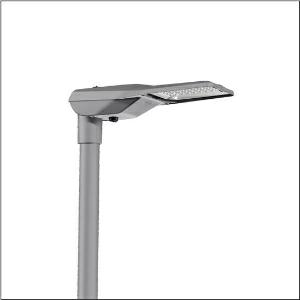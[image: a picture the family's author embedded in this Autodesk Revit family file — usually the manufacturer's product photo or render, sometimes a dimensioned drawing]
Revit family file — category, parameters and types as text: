
# Revit family: streetlight_sl_21_iq_mini___st0_8a_5xe2c31y08hb_5d56
name_source: partatom
category: Lighting Fixtures
units: mm (PartAtom-declared; Revit-internal decimal feet)

## family parameters
Cut with Voids When Loaded = No
Host = Face
Light Source = No
Part Type = Normal
Room Calculation Point = No
Round Connector Dimension = Use Diameter
Shared = No

## types (1)
- --- (1 x LED, 9750 lm, 71 W, 3000K)
    Apparent Load = 71 VA
    CIE Flux Codes = 38 75 97 100 100
    Color Rendering = 70
    Color Temperature = 3000K
    Default Elevation = 1800 mm
    Description = Streetlight SL 21 iQ mini, mast luminaire, primary light control with lens, of PMMA, primary optical cover: cover, of toughened safety glass, transparent, light distribution: ST0.8a, light emission: direct distribution, primary light characteristic: asymmetric, installation type: post-top, side-entry, LED, High Power LED, rated luminous flux: 9.750lm, luminous efficacy: 137lm/W, light colour: 730, colour temperature: 3000K, control: presetting dimming logarithmic, Street-Remote, Auto-Match, Temp-Guard, Lumen-Switch, Night-Set, Smart-Wire, Light-Fading, Desk-Remote (wireless, voltage-free reading and setting of iQ features in the workshop via application-optimized NFC function/RFID function), optimised constant luminous flux control (CLO 2.0), mains connection: 220..240V, AC, 50/60Hz, start of lifetime: 71W, end of service life: 75W, reduction: 30W, luminaire housing, of diecast aluminium, powder-coated, Siteco® metallic grey (DB 702S), corrosivity category C5 mid according to DIN EN ISO 12944, please order mast flange separately, inclination adjustable: 0°, 5°, 10°, 15°, sealing non-destructively replaceable, multi-level sealing system, length: 628mm, width: 235mm, height: 110mm, mast flange for spigot size: 42mm (side-entry): 5XC10008XM4, 60/48mm (side-entry/post-top): 5XC10108XM2, 76/60mm (side-entry/post-top): 5XC10108XM1, Smart Interface below and above, protection rating (complete): IP66, insulation class (complete): insulation class II (safety insulation), certification: CE, ENEC, ENEC+, VDE, impact resistance: IK09, permissible operating ambient temperature for outdoor applications: -40..+50°C, standard-compliant lighting for roads and squares, packaging unit: 1 piece

Light Distribution: ST0.8a
    Height = 110 mm
    Lamp = 1 x LED
    Lamp Light Flux = 9750 lm
    Lamp Power = 71 W
    Lamp count = 1
    Length = 625 mm
    Luminous efficacy = 137 lm/W
    Manufacturer = Siteco
    ModVariant = No
    Model = 5XE2C31Y08HB
    Number of Poles = 1
    OnlyDefault = Yes
    Power Factor = 1
    Product Name = Streetlight SL 21 iQ mini | ST0.8a
    Product group = mast luminaire | pylon top
    ProductGroupID = 6100
    Protection Class = Protection class II
    Protection Degree = IP 66
    RLX_Detail_Level = 1
    RLX_Emergency_Light_Flux = 0 lm
    RLX_Emergency_Type = 0
    RLX_Emergency_Type_DB = No
    RlxData = <blob elided: 92609 chars, md5=93fcecc2>
    Socket = socket
    Standby Power = 0 W
    System Light Flux = 9750 lm
    System Power = 71 W
    Type Comments = factory setting: luminous flux: 100 % | dim-lin: 254 | 716 mA
    Type Image = l_1003514.jpg
    URL = http://relux.com
    VarID = @adj_043347
    Voltage = 0 V
    Weight = 0.00 kg
    Width = 234 mm

## geometry (parser evidence)
native form markers: Blend x4, Sweep x11
no freeform markers — native parametric forms only
